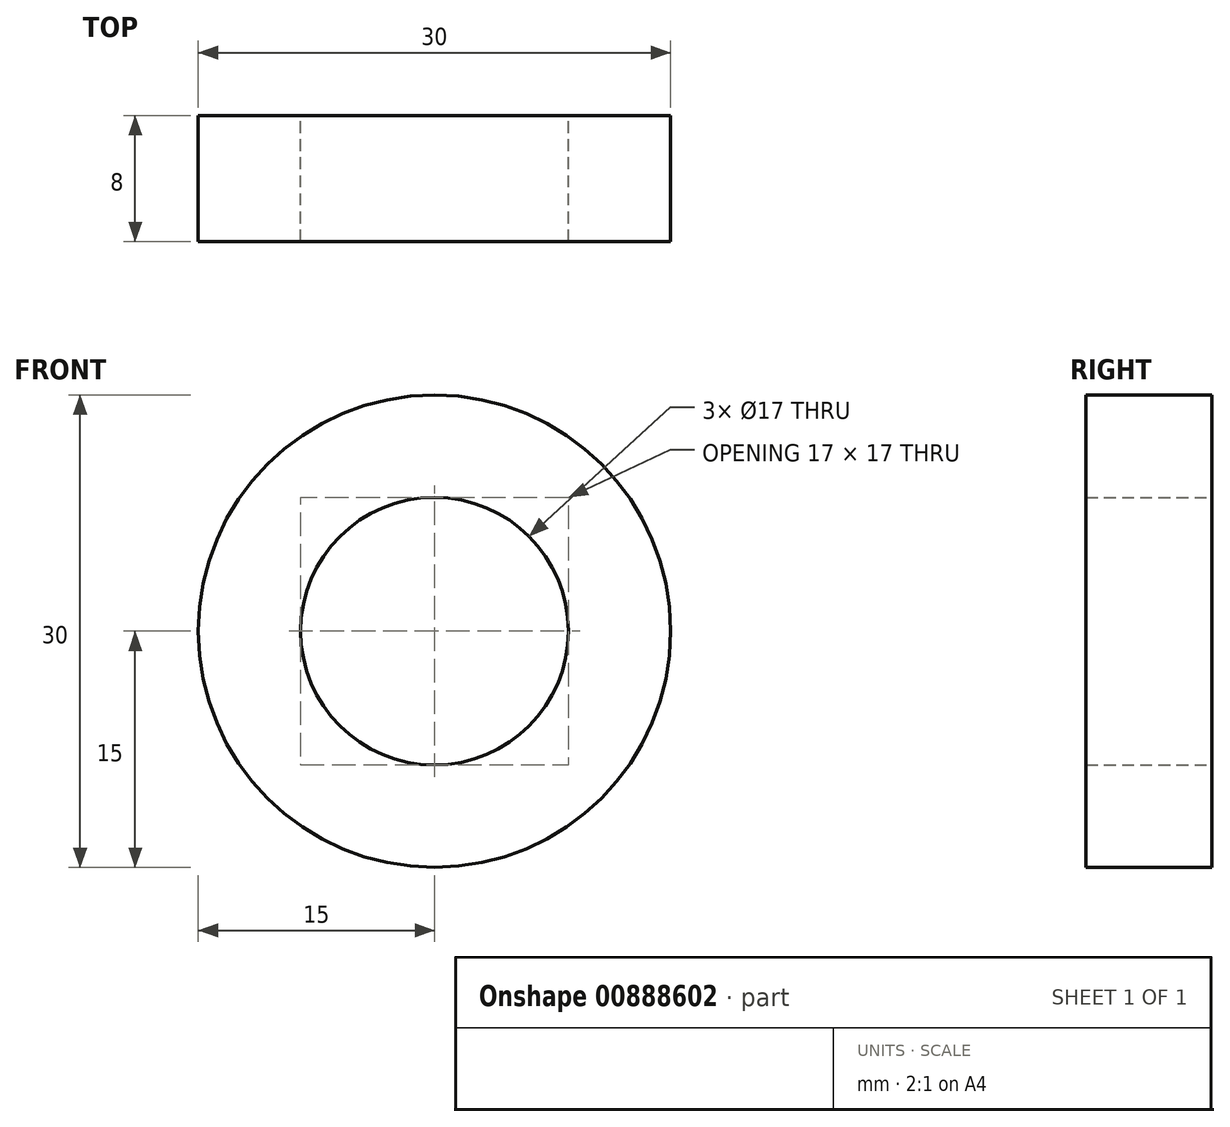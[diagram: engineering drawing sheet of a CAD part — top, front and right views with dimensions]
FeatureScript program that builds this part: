
annotation { "Feature Type Name" : "Feature", "Feature Type Description" : "" }
export const myFeature = defineFeature(function(context is Context, id is Id, definition is map)
    precondition{}
    {
        {
            var Q0;
            Q0=qCreatedBy(makeId("Front.planeOp"),FACE);
            var sketch = newSketch(context, id + "F0", { "sketchPlane" : qUnion([Q0])});
            skCircle(sketch, "E0", {"center": v(0, 0) * mm, "radius": 15 * mm});
            skSolve(sketch);
        }
        {
            var Q0;
            Q0 = qSketchRegion(id + "F0", true);
            extrude(context, id + "F1", {"entities" : qUnion([Q0]), "oppositeDirection" : true, "depth" : 8 * mm, "offsetDistance" : 25 * mm});
        }
        {
            var Q0;
            Q0=makeQuery(id+"F1.opExtrude","CAP_FACE",FACE,{"disambiguationData":[OSD([sQuery(id+"F0.wireOp",EDGE,"E0")])],"isStart":false});
            var sketch = newSketch(context, id + "F2", { "sketchPlane" : qUnion([Q0])});
            skCircle(sketch, "E1", {"center": v(0, 0) * mm, "radius": 8.5 * mm});
            skSolve(sketch);
        }
        {
            var Q0;
            Q0=makeQuery(id+"F2.imprint","IMPRINT",FACE,{"disambiguationData":[TD([[makeQuery(id+"F2.imprint","IMPRINT",EDGE,{"derivedFrom":sQuery(id+"F2.wireOp",EDGE,"E1")}),1.0]])]});
            extrude(context, id + "F3", {"entities" : qUnion([Q0]), "operationType" : NewBodyOperationType.REMOVE, "oppositeDirection" : true, "depth" : 25 * mm, "offsetDistance" : 25 * mm});
        }
    });
